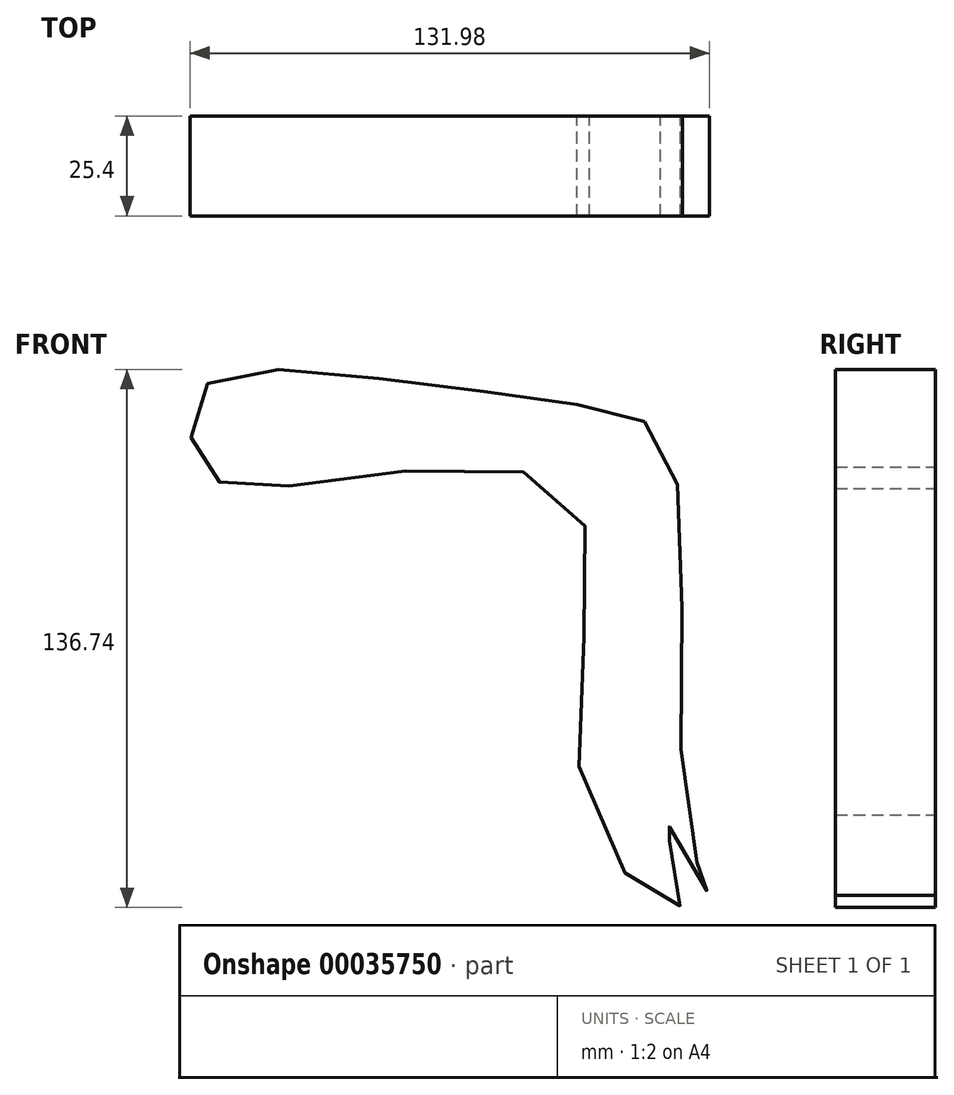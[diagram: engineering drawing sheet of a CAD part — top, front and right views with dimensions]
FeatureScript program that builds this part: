
annotation { "Feature Type Name" : "Feature", "Feature Type Description" : "" }
export const myFeature = defineFeature(function(context is Context, id is Id, definition is map)
    precondition{}
    {
        {
            var Q0;
            Q0=qCreatedBy(makeId("Front.planeOp"),FACE);
            var sketch = newSketch(context, id + "F0", { "sketchPlane" : qUnion([Q0])});
            skFitSpline(sketch, "E0", {"points": [v(-53.7, 29.45) * mm, v(-75.79, 34.21) * mm, v(-76.22, 53.7) * mm, v(-38.54, 57.6) * mm, v(21.65, 49.8) * mm, v(42.87, 38.1) * mm, v(47.64, -56.73) * mm, v(52.83, -74.05) * mm, v(40.7, -54.13) * mm, v(46.34, -76.22) * mm, v(22.09, -51.97) * mm, v(17.76, 26.85) * mm, v(-53.7, 29.45) * mm]});
            skSolve(sketch);
        }
        {
            var Q0;
            Q0=makeQuery(id+"F0.imprint","IMPRINT",FACE,{"disambiguationData":[TD([[makeQuery(id+"F0.imprint","IMPRINT",EDGE,{"derivedFrom":sQuery(id+"F0.wireOp",EDGE,"E0")}),-1.0]])]});
            extrude(context, id + "F1", {"entities" : qUnion([Q0]), "depth" : 25.4 * mm});
        }
    });
